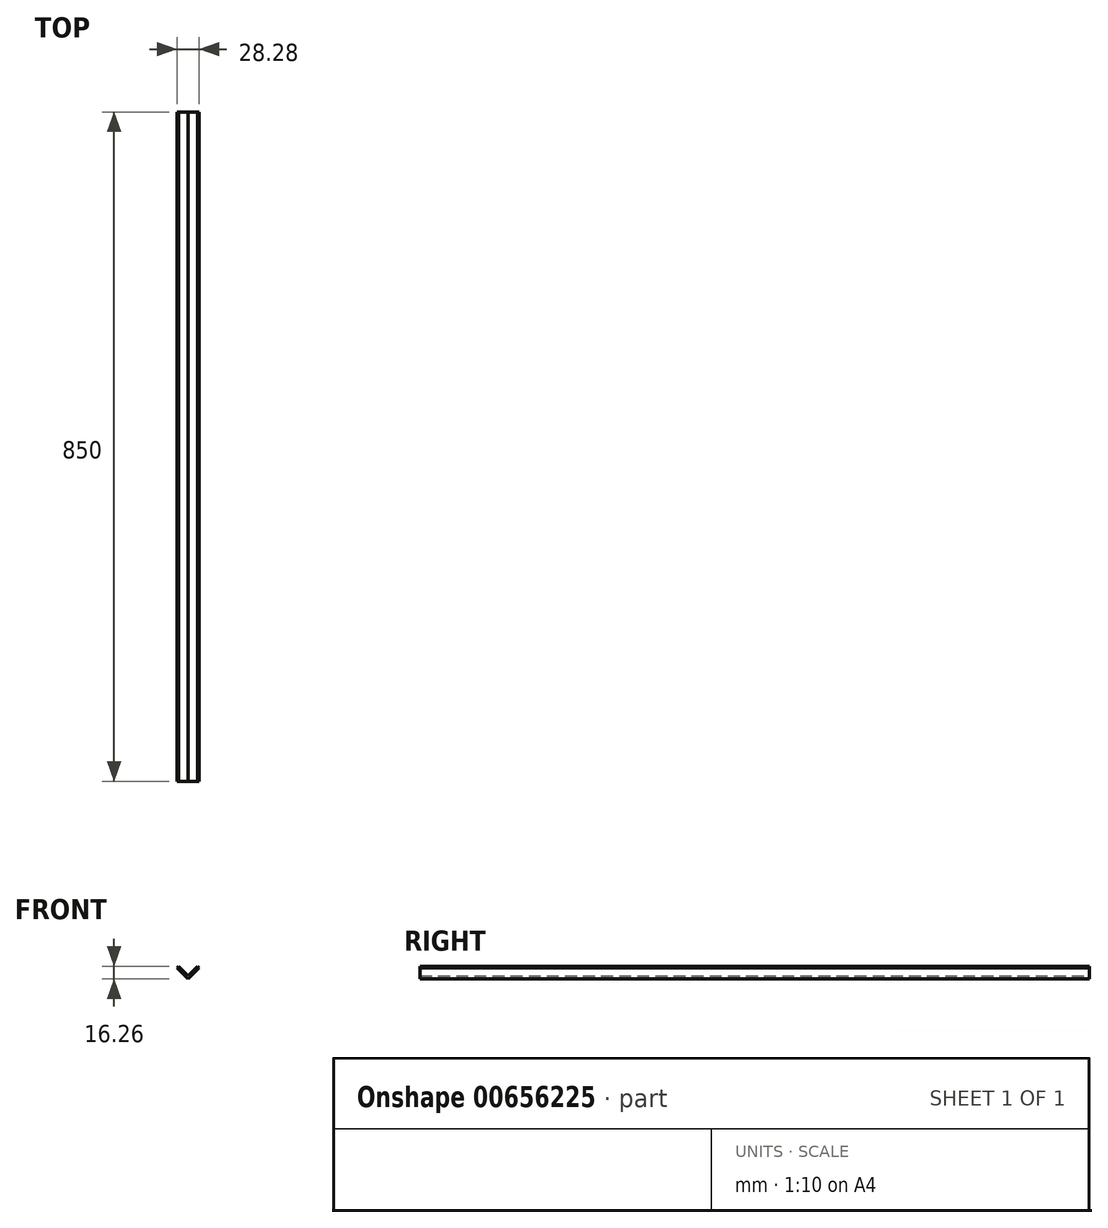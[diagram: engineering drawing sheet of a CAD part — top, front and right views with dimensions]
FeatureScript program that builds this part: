
annotation { "Feature Type Name" : "Feature", "Feature Type Description" : "" }
export const myFeature = defineFeature(function(context is Context, id is Id, definition is map)
    precondition{}
    {
        {
            var Q0;
            Q0=qCreatedBy(makeId("Front.planeOp"),FACE);
            var sketch = newSketch(context, id + "F0", { "sketchPlane" : qUnion([Q0])});
            skLineSegment(sketch, "E0", {"start": v(0, 0) * mm, "end": v(-12.02, 12.02) * mm});
            skLineSegment(sketch, "E1", {"start": v(-12.02, 12.02) * mm, "end": v(-14.14, 9.9) * mm});
            skLineSegment(sketch, "E2", {"start": v(-14.14, 9.9) * mm, "end": v(0, -4.24) * mm});
            skLineSegment(sketch, "E3", {"start": v(0, -4.24) * mm, "end": v(0, 0) * mm, "construction": true});
            skLineSegment(sketch, "E4.MirrorCS", {"start": v(0, 0) * mm, "end": v(12.02, 12.02) * mm});
            skLineSegment(sketch, "E5.MirrorCS", {"start": v(12.02, 12.02) * mm, "end": v(14.14, 9.9) * mm});
            skLineSegment(sketch, "E6.MirrorCS", {"start": v(14.14, 9.9) * mm, "end": v(0, -4.24) * mm});
            skSolve(sketch);
        }
        {
            var Q0;
            Q0=makeQuery(id+"F0.imprint","IMPRINT",FACE,{"disambiguationData":[TD([[makeQuery(id+"F0.imprint","IMPRINT",EDGE,{"derivedFrom":sQuery(id+"F0.wireOp",EDGE,"E0")}),1.0]])]});
            extrude(context, id + "F1", {"entities" : qUnion([Q0]), "flatOperationType" : FlatOperationType.REMOVE, "depth" : (900 - 50) * mm, "offsetDistance" : 25.4 * mm, "domain" : OperationDomain.MODEL});
        }
    });
